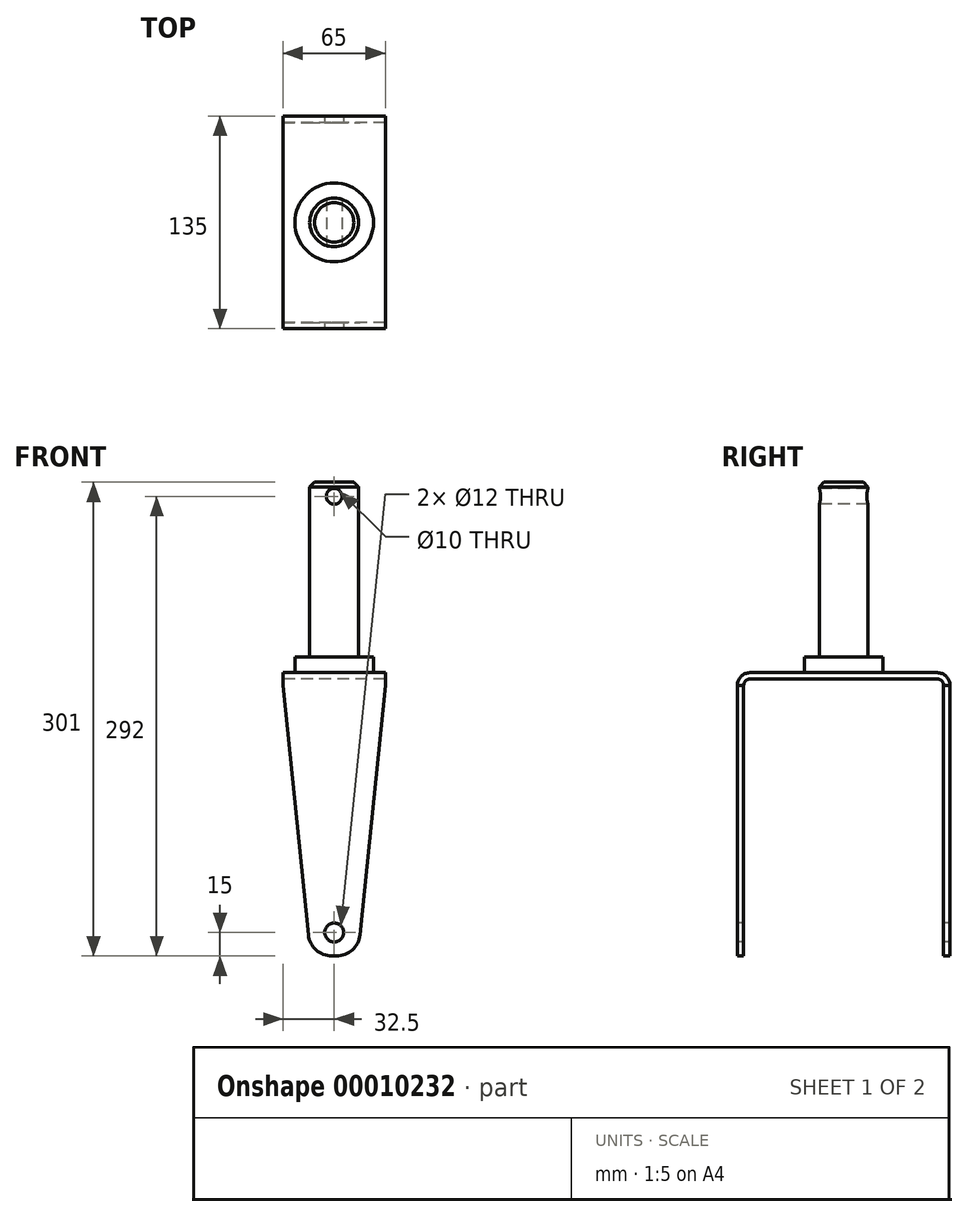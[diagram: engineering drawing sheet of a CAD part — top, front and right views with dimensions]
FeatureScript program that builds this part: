
annotation { "Feature Type Name" : "Feature", "Feature Type Description" : "" }
export const myFeature = defineFeature(function(context is Context, id is Id, definition is map)
    precondition{}
    {
        {
            var Q0;
            Q0=qCreatedBy(makeId("Right.planeOp"),FACE);
            var sketch = newSketch(context, id + "F0", { "sketchPlane" : qUnion([Q0])});
            skLineSegment(sketch, "E0", {"start": v(0, 165) * mm, "end": v(-59.5, 165) * mm});
            skLineSegment(sketch, "E1", {"start": v(-67.5, 157) * mm, "end": v(-67.5, -15) * mm});
            skLineSegment(sketch, "E2", {"start": v(-67.5, -15) * mm, "end": v(-63.5, -15) * mm});
            skLineSegment(sketch, "E3", {"start": v(-63.5, -15) * mm, "end": v(-63.5, 157) * mm});
            skLineSegment(sketch, "E4", {"start": v(-59.5, 161) * mm, "end": v(0, 161) * mm});
            skPoint(sketch, "E5.visualSharp", {"position": v(-63.5, 161) * mm});
            skArc(sketch, "E5.filletArc", {"start": v(-59.5, 161) * mm, "mid": v(-62.33, 159.83) * mm, "end": v(-63.5, 157) * mm});
            skPoint(sketch, "E6.visualSharp", {"position": v(-67.5, 165) * mm});
            skArc(sketch, "E6.filletArc", {"start": v(-59.5, 165) * mm, "mid": v(-65.16, 162.66) * mm, "end": v(-67.5, 157) * mm});
            skArc(sketch, "E7.0.MirrorCS", {"start": v(59.5, 161) * mm, "mid": v(62.33, 159.83) * mm, "end": v(63.5, 157) * mm});
            skLineSegment(sketch, "E7.1.MirrorCS", {"start": v(67.5, -15) * mm, "end": v(63.5, -15) * mm});
            skArc(sketch, "E7.2.MirrorCS", {"start": v(59.5, 165) * mm, "mid": v(65.16, 162.66) * mm, "end": v(67.5, 157) * mm});
            skLineSegment(sketch, "E7.3.MirrorCS", {"start": v(67.5, 157) * mm, "end": v(67.5, -15) * mm});
            skLineSegment(sketch, "E7.4.MirrorCS", {"start": v(0, 165) * mm, "end": v(59.5, 165) * mm});
            skLineSegment(sketch, "E7.5.MirrorCS", {"start": v(59.5, 161) * mm, "end": v(0, 161) * mm});
            skLineSegment(sketch, "E7.6.MirrorCS", {"start": v(63.5, -15) * mm, "end": v(63.5, 157) * mm});
            skPoint(sketch, "E7.7.MirrorP", {"position": v(63.5, 161) * mm});
            skPoint(sketch, "E7.8.MirrorP", {"position": v(67.5, 165) * mm});
            skSolve(sketch);
        }
        {
            var Q0;
            Q0 = qSketchRegion(id + "F0", true);
            extrude(context, id + "F1", {"entities" : qUnion([Q0]), "endBound" : BoundingType.SYMMETRIC, "depth" : 65 * mm});
        }
        {
            var Q0;
            Q0=makeQuery(id+"F1.opExtrude","CAP_EDGE",EDGE,{"disambiguationData":[OSD([sQuery(id+"F0.wireOp",EDGE,"E2")])],"isStart":true});
            chamfer(context, id + "F2", {"entities" : qUnion([Q0]), "chamferType" : ChamferType.TWO_OFFSETS, "width1" : 17.5 * mm, "oppositeDirection" : false, "width2" : 172 * mm, "tangentPropagation" : true});
        }
        {
            var Q0;
            Q0=makeQuery(id+"F1.opExtrude","CAP_EDGE",EDGE,{"disambiguationData":[OSD([sQuery(id+"F0.wireOp",EDGE,"E2")])],"isStart":false});
            chamfer(context, id + "F3", {"entities" : qUnion([Q0]), "chamferType" : ChamferType.TWO_OFFSETS, "width1" : 172 * mm, "oppositeDirection" : false, "width2" : 17.5 * mm, "tangentPropagation" : true});
        }
        {
            var Q0;
            {var subQ0=sQuery(id+"F0.wireOp",EDGE,"E2");Q0=makeQuery(id+"F3.opChamfer","BLEND_EDGE",EDGE,{"blendedFrom":[makeQuery(id+"F1.opExtrude","CAP_EDGE",EDGE,{"disambiguationData":[OSD([subQ0])],"isStart":false}),makeQuery(id+"F1.opExtrude","SWEPT_FACE",FACE,{"disambiguationData":[OSD([subQ0])]})],"blendedInto":[makeQuery(id+"F1.opExtrude","SWEPT_FACE",FACE,{"disambiguationData":[OSD([subQ0])]})]});}
            fillet(context, id + "F4", {"entities" : qUnion([Q0]), "radius" : 15 * mm, "tangentPropagation" : true, "allowEdgeOverflow" : false});
        }
        {
            var Q0;
            {var subQ0=sQuery(id+"F0.wireOp",EDGE,"E2");Q0=makeQuery(id+"F2.opChamfer","BLEND_EDGE",EDGE,{"blendedFrom":[makeQuery(id+"F1.opExtrude","CAP_EDGE",EDGE,{"disambiguationData":[OSD([subQ0])],"isStart":true}),makeQuery(id+"F1.opExtrude","SWEPT_FACE",FACE,{"disambiguationData":[OSD([subQ0])]})],"blendedInto":[makeQuery(id+"F1.opExtrude","SWEPT_FACE",FACE,{"disambiguationData":[OSD([subQ0])]})]});}
            fillet(context, id + "F5", {"entities" : qUnion([Q0]), "radius" : 15 * mm, "tangentPropagation" : true, "allowEdgeOverflow" : false});
        }
        {
            var Q0;
            Q0=makeQuery(id+"F1.opExtrude","CAP_EDGE",EDGE,{"disambiguationData":[OSD([sQuery(id+"F0.wireOp",EDGE,"E7.1.MirrorCS")])],"isStart":false});
            chamfer(context, id + "F6", {"entities" : qUnion([Q0]), "chamferType" : ChamferType.TWO_OFFSETS, "width1" : 17.5 * mm, "oppositeDirection" : false, "width2" : 172 * mm, "tangentPropagation" : true});
        }
        {
            var Q0;
            Q0=makeQuery(id+"F1.opExtrude","CAP_EDGE",EDGE,{"disambiguationData":[OSD([sQuery(id+"F0.wireOp",EDGE,"E7.1.MirrorCS")])],"isStart":true});
            chamfer(context, id + "F7", {"entities" : qUnion([Q0]), "chamferType" : ChamferType.TWO_OFFSETS, "width1" : 172 * mm, "oppositeDirection" : false, "width2" : 17.5 * mm, "tangentPropagation" : true});
        }
        {
            var Q0;
            {var subQ0=sQuery(id+"F0.wireOp",EDGE,"E7.1.MirrorCS");Q0=makeQuery(id+"F7.opChamfer","BLEND_EDGE",EDGE,{"blendedFrom":[makeQuery(id+"F1.opExtrude","CAP_EDGE",EDGE,{"disambiguationData":[OSD([subQ0])],"isStart":true}),makeQuery(id+"F1.opExtrude","SWEPT_FACE",FACE,{"disambiguationData":[OSD([subQ0])]})],"blendedInto":[makeQuery(id+"F1.opExtrude","SWEPT_FACE",FACE,{"disambiguationData":[OSD([subQ0])]})]});}
            var Q1;
            {var subQ0=sQuery(id+"F0.wireOp",EDGE,"E7.1.MirrorCS");Q1=makeQuery(id+"F6.opChamfer","BLEND_EDGE",EDGE,{"blendedFrom":[makeQuery(id+"F1.opExtrude","CAP_EDGE",EDGE,{"disambiguationData":[OSD([subQ0])],"isStart":false}),makeQuery(id+"F1.opExtrude","SWEPT_FACE",FACE,{"disambiguationData":[OSD([subQ0])]})],"blendedInto":[makeQuery(id+"F1.opExtrude","SWEPT_FACE",FACE,{"disambiguationData":[OSD([subQ0])]})]});}
            fillet(context, id + "F8", {"entities" : qUnion([Q0, Q1]), "radius" : 15 * mm, "tangentPropagation" : true, "allowEdgeOverflow" : false});
        }
        {
            var Q0;
            Q0=qCreatedBy(makeId("Front.planeOp"),FACE);
            var sketch = newSketch(context, id + "F9", { "sketchPlane" : qUnion([Q0])});
            skCircle(sketch, "E8", {"center": v(0, 0) * mm, "radius": 6 * mm});
            skSolve(sketch);
        }
        {
            var Q0;
            Q0 = qSketchRegion(id + "F9", true);
            extrude(context, id + "F10", {"entities" : qUnion([Q0]), "operationType" : NewBodyOperationType.REMOVE, "endBound" : BoundingType.SYMMETRIC, "oppositeDirection" : true, "depth" : 135 * mm});
        }
        {
            var Q0;
            Q0=makeQuery(id+"F1.opExtrude","SWEPT_FACE",FACE,{"disambiguationData":[OSD([sQuery(id+"F0.wireOp",EDGE,"E0"),sQuery(id+"F0.wireOp",EDGE,"E7.4.MirrorCS")])]});
            var sketch = newSketch(context, id + "F11", { "sketchPlane" : qUnion([Q0])});
            skCircle(sketch, "E9", {"center": v(0, 0) * mm, "radius": 15.5 * mm});
            skSolve(sketch);
        }
        {
            var Q0;
            Q0=makeQuery(id+"F11.imprint","IMPRINT",FACE,{"disambiguationData":[TD([[makeQuery(id+"F11.imprint","IMPRINT",EDGE,{"derivedFrom":sQuery(id+"F11.wireOp",EDGE,"E9")}),1.0]])]});
            extrude(context, id + "F12", {"entities" : qUnion([Q0]), "operationType" : NewBodyOperationType.ADD, "depth" : 121 * mm});
        }
        {
            var Q0;
            Q0=makeQuery(id+"F1.opExtrude","SWEPT_FACE",FACE,{"disambiguationData":[OSD([sQuery(id+"F0.wireOp",EDGE,"E0"),sQuery(id+"F0.wireOp",EDGE,"E7.4.MirrorCS")])]});
            var sketch = newSketch(context, id + "F13", { "sketchPlane" : qUnion([Q0])});
            skCircle(sketch, "E10", {"center": v(0, 0) * mm, "radius": 25 * mm});
            skSolve(sketch);
        }
        {
            var Q0;
            Q0=makeQuery(id+"F13.imprint","IMPRINT",FACE,{"disambiguationData":[TD([[makeQuery(id+"F13.imprint","IMPRINT",EDGE,{"derivedFrom":sQuery(id+"F13.wireOp",EDGE,"E10")}),1.0]])]});
            extrude(context, id + "F14", {"entities" : qUnion([Q0]), "operationType" : NewBodyOperationType.ADD, "depth" : 10 * mm});
        }
        {
            var Q0;
            Q0=qCreatedBy(makeId("Front.planeOp"),FACE);
            var sketch = newSketch(context, id + "F15", { "sketchPlane" : qUnion([Q0])});
            skCircle(sketch, "E11", {"center": v(0, 277) * mm, "radius": 5 * mm});
            skSolve(sketch);
        }
        {
            var Q0;
            Q0 = qSketchRegion(id + "F15", true);
            extrude(context, id + "F16", {"entities" : qUnion([Q0]), "operationType" : NewBodyOperationType.REMOVE, "endBound" : BoundingType.SYMMETRIC, "oppositeDirection" : true, "depth" : 31 * mm});
        }
        {
            var Q0;
            Q0=makeQuery(id+"F12.opExtrude","CAP_EDGE",EDGE,{"disambiguationData":[OSD([sQuery(id+"F11.wireOp",EDGE,"E9")])],"isStart":false});
            chamfer(context, id + "F17", {"entities" : qUnion([Q0]), "width" : 3 * mm, "tangentPropagation" : true});
        }
    });
